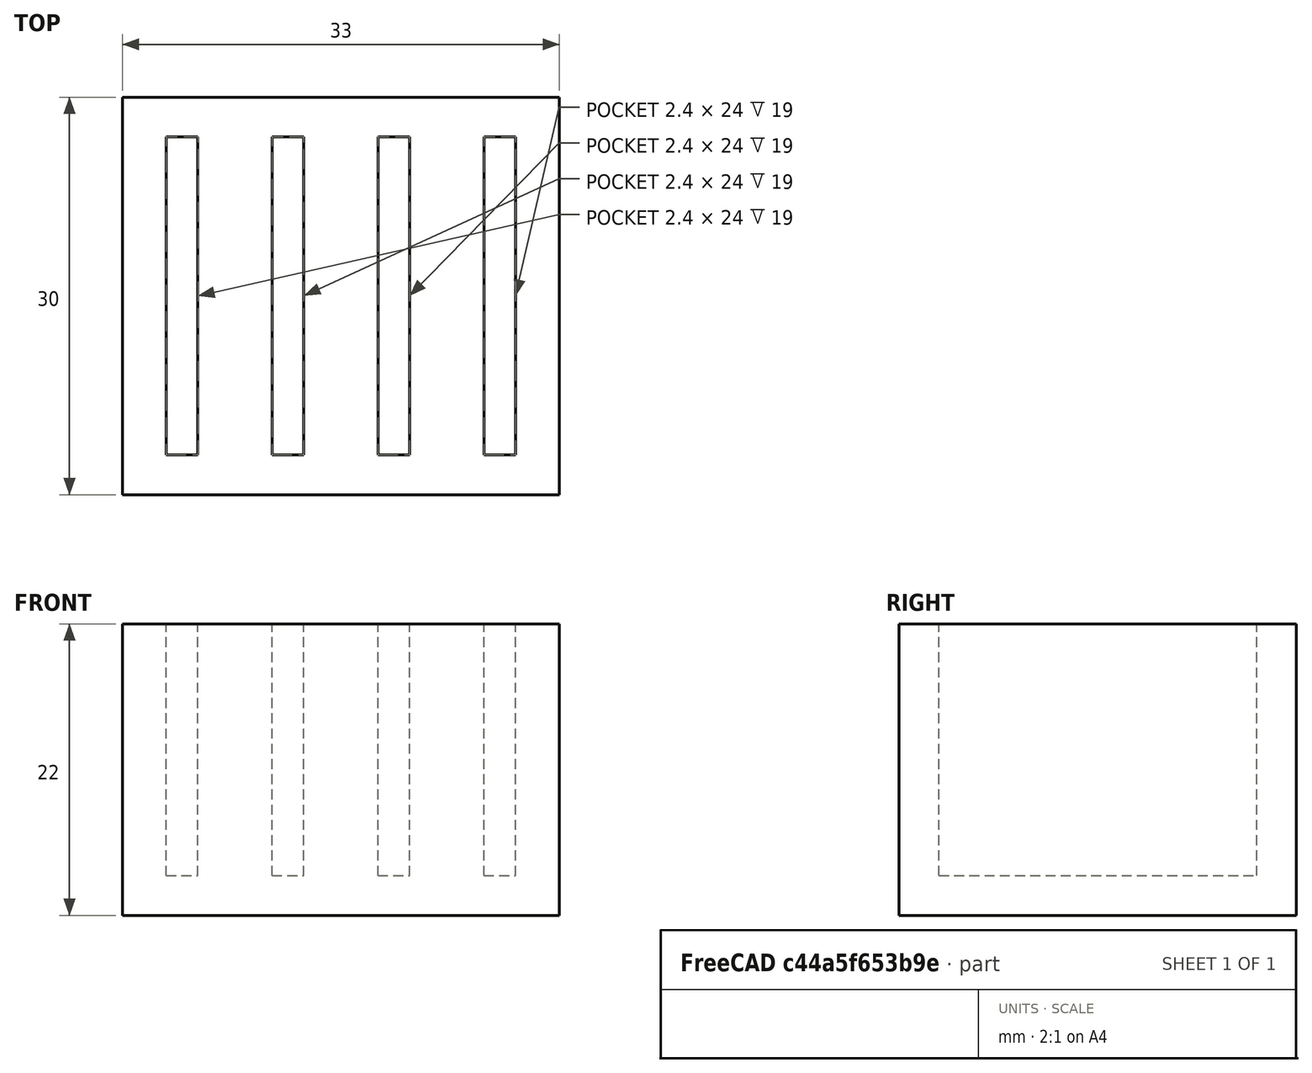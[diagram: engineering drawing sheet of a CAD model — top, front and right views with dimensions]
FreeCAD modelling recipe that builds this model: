
FCSTD DOCUMENT  (FreeCAD 0.18.4R)
Label: tutorial_freecad_ex08_b
License: All rights reserved
LicenseURL: http://en.wikipedia.org/wiki/All_rights_reserved
objects: Part::Box×5, Part::MultiFuse×1, Part::Cut×1
note: 7 computed .brp shape members not serialized (recipe doc carries the construction recipe); baked Part::Feature solids carry a one-line shape summary decoded from their .brp

FEATURE [Part::Box] Box  label="base"
  AttacherType = Attacher::AttachEngine3D
  Height = 22
  Length = 33
  Placement = pos=(-16.5,-15,0) rot=(0,1,0;0rad)
  Width = 30
FEATURE [Part::Box] Box001  label="ranura_001"
  AttacherType = Attacher::AttachEngine3D
  Height = 24
  Length = 2.4
  Width = 24
FEATURE [Part::Box] Box002  label="ranura_002"
  AttacherType = Attacher::AttachEngine3D
  Height = 24
  Length = 2.4
  Placement = pos=(8,0,0) rot=(0,0,1;0rad)
  Width = 24
FEATURE [Part::Box] Box003  label="ranura_003"
  AttacherType = Attacher::AttachEngine3D
  Height = 24
  Length = 2.4
  Placement = pos=(16,0,0) rot=(0,0,1;0rad)
  Width = 24
FEATURE [Part::Box] Box004  label="ranura_004"
  AttacherType = Attacher::AttachEngine3D
  Height = 24
  Length = 2.4
  Placement = pos=(24,0,0) rot=(0,0,1;0rad)
  Width = 24
FEATURE [Part::MultiFuse] Fusion  label="ranuras_sd"
  Placement = pos=(-13.2,-12,3) rot=(0,0,1;0rad)
  Refine = true
  Shapes = -> [Box004,Box001,Box002,Box003]
FEATURE [Part::Cut] Cut  label="porta_sd"
  Base = -> Box
  Placement = pos=(16.5,15,0) rot=(0,0,1;0rad)
  Refine = true
  Tool = -> Fusion
